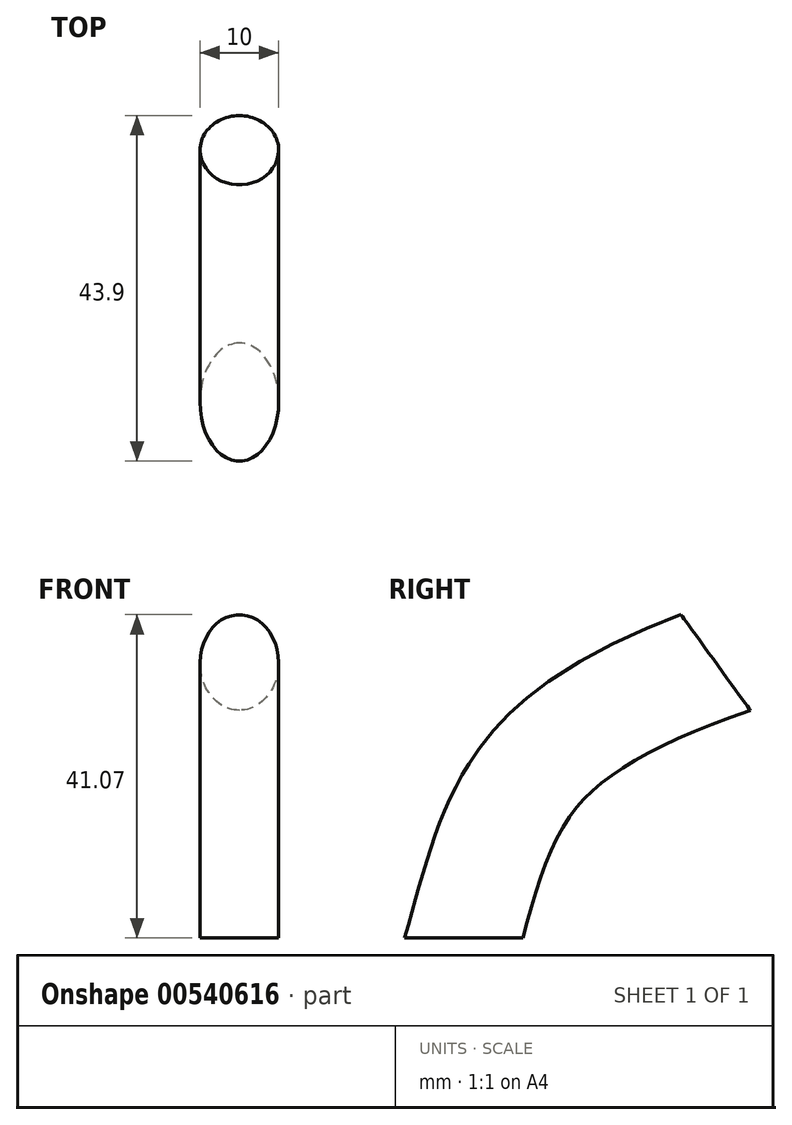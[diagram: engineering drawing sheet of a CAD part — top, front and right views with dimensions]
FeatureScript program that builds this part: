
annotation { "Feature Type Name" : "Feature", "Feature Type Description" : "" }
export const myFeature = defineFeature(function(context is Context, id is Id, definition is map)
    precondition{}
    {
        {
            var Q0;
            Q0=qCreatedBy(makeId("Right.planeOp"),FACE);
            var sketch = newSketch(context, id + "F0", { "sketchPlane" : qUnion([Q0])});
            skFitSpline(sketch, "E0", {"points": [v(0, 0) * mm, v(8, 20) * mm, v(32, 35) * mm], "startDerivative": vector(12.88, 45.07) * mm, "endDerivative": vector(61.79, 22.47) * mm});
            skSolve(sketch);
        }
        {
            var Q0;
            Q0=qCreatedBy(makeId("Top.planeOp"),FACE);
            var sketch = newSketch(context, id + "F1", { "sketchPlane" : qUnion([Q0])});
            skEllipse(sketch, "E1", {"center": v(0, 0) * mm, "majorRadius": 7.5 * mm, "minorRadius": 5 * mm, "majorAxis": v(0, 1)});
            skSolve(sketch);
        }
        {
            var Q0;
            Q0=makeQuery(id+"F1.imprint","IMPRINT",FACE,{"disambiguationData":[TD([[makeQuery(id+"F1.imprint","IMPRINT",EDGE,{"derivedFrom":sQuery(id+"F1.wireOp",EDGE,"E1")}),1.0]])]});
            var Q1;
            Q1=sQuery(id+"F0.wireOp",EDGE,"E0");
            sweep(context, id + "F2", {"profiles" : qUnion([Q0]), "path" : qUnion([Q1])});
        }
    });
